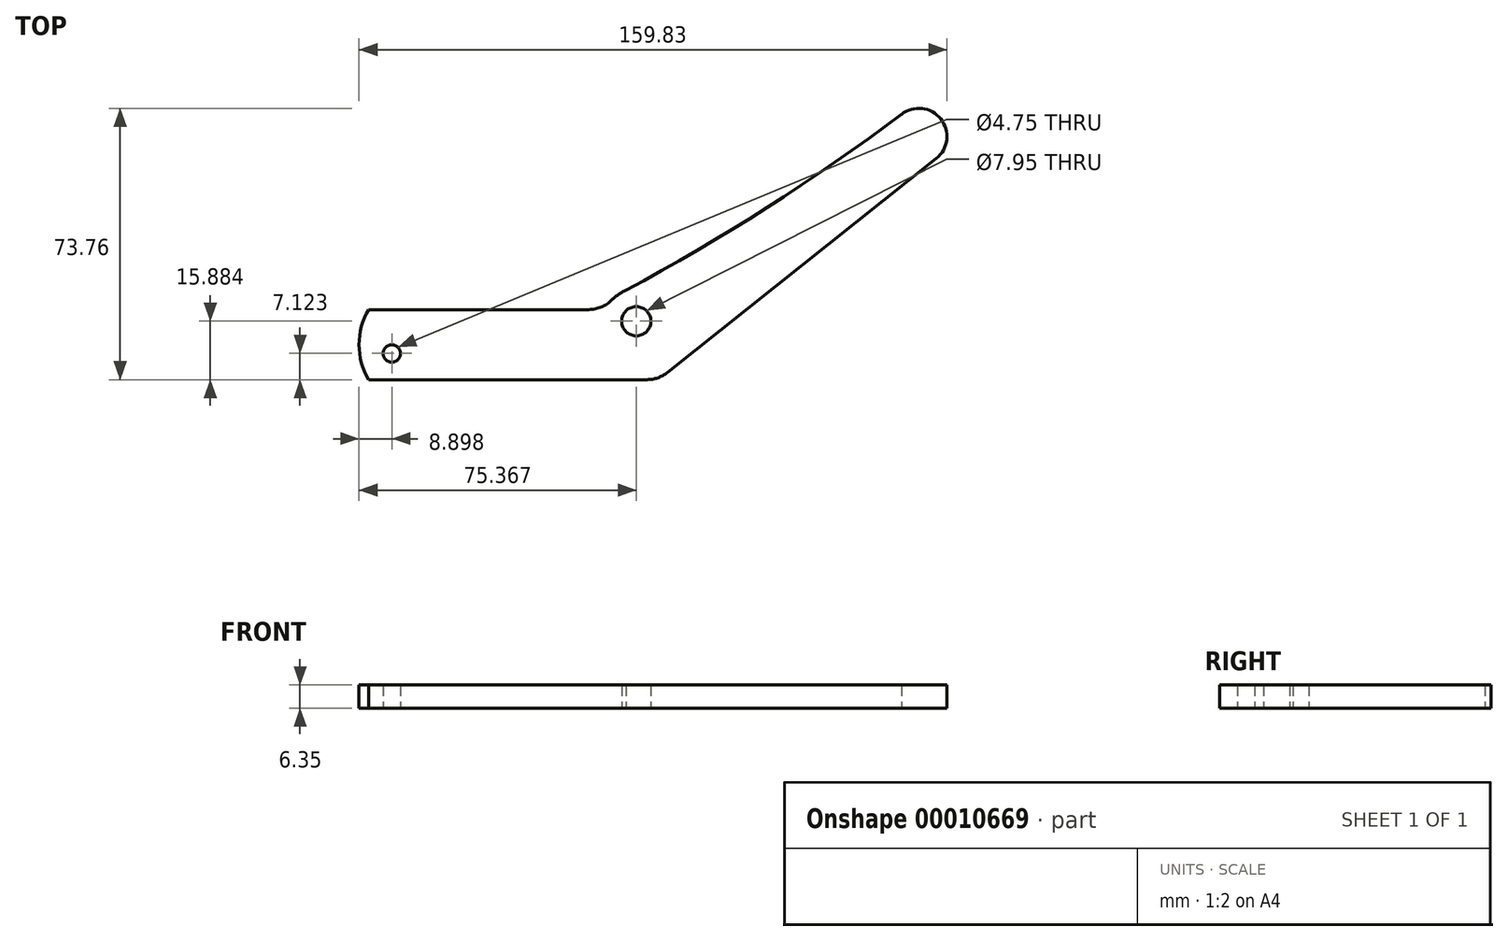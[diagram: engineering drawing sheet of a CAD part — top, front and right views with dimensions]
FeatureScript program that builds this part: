
annotation { "Feature Type Name" : "Feature", "Feature Type Description" : "" }
export const myFeature = defineFeature(function(context is Context, id is Id, definition is map)
    precondition{}
    {
        {
            var Q0;
            Q0=qCreatedBy(makeId("Top.planeOp"), FACE);
            var sketch = newSketch(context, id + "F0", { "sketchPlane" : qUnion([Q0])});
            skLineSegment(sketch, "E0", {"start": v(76.78, 61.07) * mm, "end": v(0, 0) * mm, "construction": true});
            skLineSegment(sketch, "E1", {"start": v(0, 0) * mm, "end": v(-60.33, 0) * mm, "construction": true});
            skSolve(sketch);
        }
        {
            var Q0;
            Q0=qCreatedBy(makeId("Top.planeOp"), FACE);
            var sketch = newSketch(context, id + "F1", { "sketchPlane" : qUnion([Q0])});
            skCircle(sketch, "E2", {"center": v(-0.05, 10.82) * mm, "radius": 3.98 * mm});
            skCircle(sketch, "E3", {"center": v(-66.52, 2.06) * mm, "radius": 2.37 * mm});
            skArc(sketch, "E4", {"start": v(81.53, 55.1) * mm, "mid": v(82.75, 65.82) * mm, "end": v(72.03, 67.04) * mm});
            skLineSegment(sketch, "E5", {"start": v(81.53, 55.1) * mm, "end": v(8.41, -3.13) * mm});
            skLineSegment(sketch, "E6", {"start": v(2.87, -5.06) * mm, "end": v(-72.87, -5.06) * mm});
            skLineSegment(sketch, "E7", {"start": v(72.03, 67.04) * mm, "end": v(81.53, 55.1) * mm, "construction": true});
            skArc(sketch, "E8", {"start": v(-72.87, 13.99) * mm, "mid": v(-75.42, 4.46) * mm, "end": v(-72.87, -5.06) * mm});
            skArc(sketch, "E9", {"start": v(-2.87, 19.2) * mm, "mid": v(-4.91, 18.07) * mm, "end": v(-6.71, 16.58) * mm});
            skLineSegment(sketch, "E10", {"start": v(-12.99, 13.99) * mm, "end": v(-72.87, 13.99) * mm});
            skPoint(sketch, "E11.visualSharp", {"position": v(5.98, -5.06) * mm});
            skArc(sketch, "E11.filletArc", {"start": v(2.87, -5.06) * mm, "mid": v(5.8, -4.56) * mm, "end": v(8.41, -3.13) * mm});
            skPoint(sketch, "E12.visualSharp", {"position": v(-8.71, 13.99) * mm});
            skArc(sketch, "E12.filletArc", {"start": v(-12.99, 13.99) * mm, "mid": v(-9.6, 14.66) * mm, "end": v(-6.71, 16.58) * mm});
            skArc(sketch, "E13", {"start": v(-4.56, 18.3) * mm, "mid": v(34.67, 41.2) * mm, "end": v(72.03, 67.04) * mm});
            skSolve(sketch);
        }
        {
            var Q0;
            Q0 = qSketchRegion(id + "F1", true);
            extrude(context, id + "F2", {"entities" : qUnion([Q0]), "depth" : 6.35 * mm, "offsetDistance" : 25.4 * mm});
        }
    });
